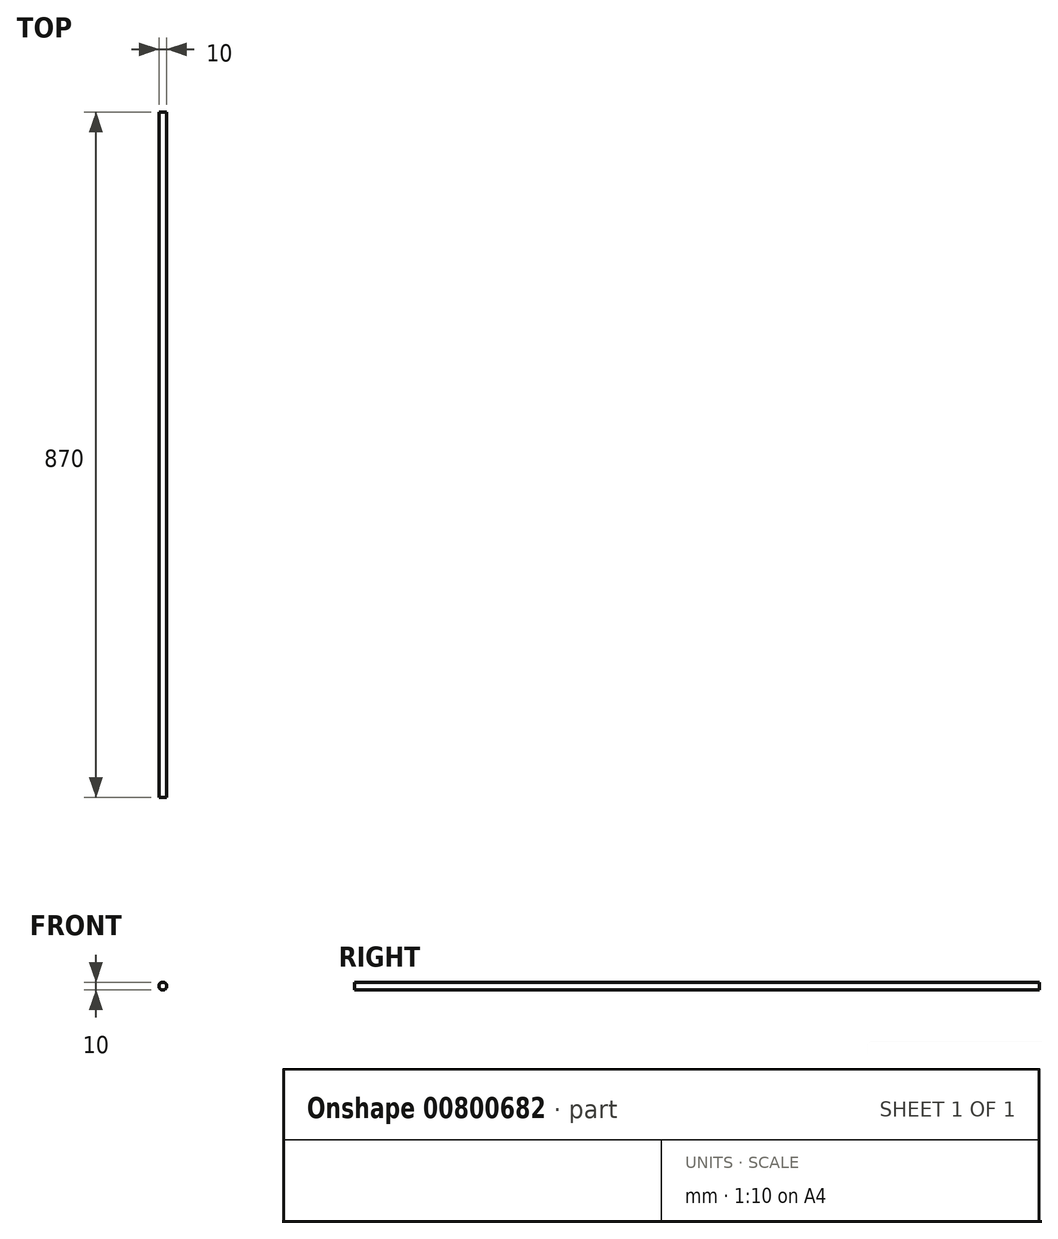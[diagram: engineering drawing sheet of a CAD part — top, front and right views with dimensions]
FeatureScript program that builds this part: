
annotation { "Feature Type Name" : "Feature", "Feature Type Description" : "" }
export const myFeature = defineFeature(function(context is Context, id is Id, definition is map)
    precondition{}
    {
        {
            var Q0;
            Q0=qCreatedBy(makeId("Front.planeOp"),FACE);
            var sketch = newSketch(context, id + "F0", { "sketchPlane" : qUnion([Q0])});
            skCircle(sketch, "E0", {"center": v(0, 0) * mm, "radius": 5 * mm});
            skSolve(sketch);
        }
        {
            var Q0;
            Q0=makeQuery(id+"F0.imprint","IMPRINT",FACE,{"disambiguationData":[TD([[makeQuery(id+"F0.imprint","IMPRINT",EDGE,{"derivedFrom":sQuery(id+"F0.wireOp",EDGE,"E0")}),1.0]])]});
            extrude(context, id + "F1", {"entities" : qUnion([Q0]), "endBound" : BoundingType.SYMMETRIC, "depth" : 870 * mm, "offsetDistance" : 25 * mm});
        }
    });
